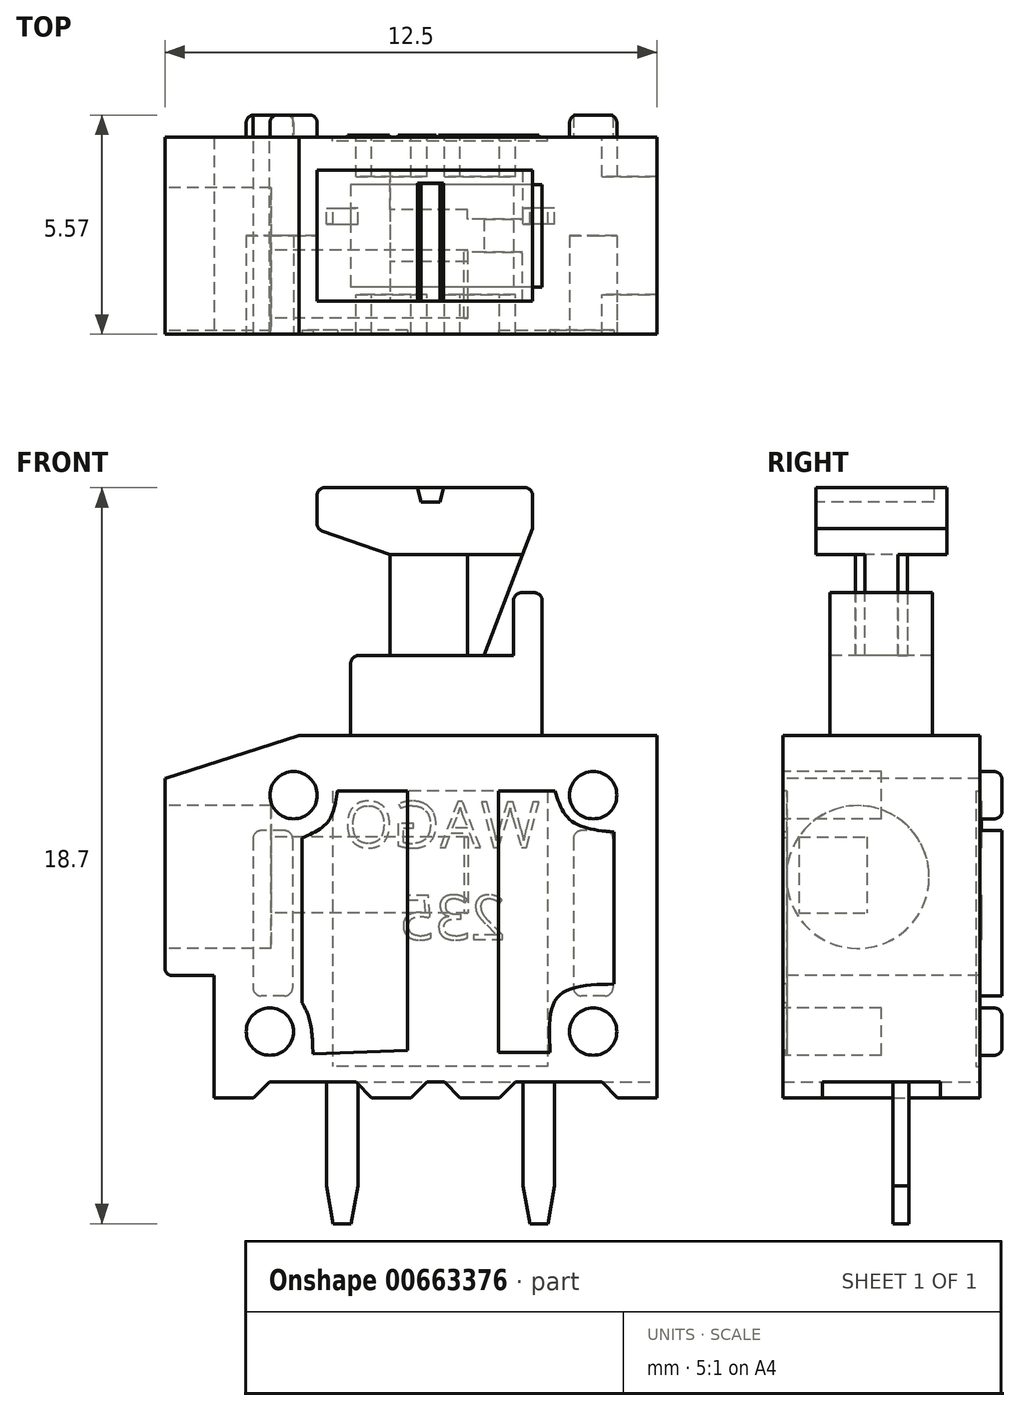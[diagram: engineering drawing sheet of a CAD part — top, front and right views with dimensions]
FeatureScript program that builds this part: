
annotation { "Feature Type Name" : "Feature", "Feature Type Description" : "" }
export const myFeature = defineFeature(function(context is Context, id is Id, definition is map)
    precondition{}
    {
        {
            var Q0;
            Q0=qCreatedBy(makeId("Front.planeOp"),FACE);
            var sketch = newSketch(context, id + "F0", { "sketchPlane" : qUnion([Q0])});
            skLineSegment(sketch, "E0", {"start": v(-5.72, 0) * mm, "end": v(6.78, 0) * mm});
            skLineSegment(sketch, "E1", {"start": v(6.78, 0) * mm, "end": v(6.78, 9.2) * mm});
            skLineSegment(sketch, "E2", {"start": v(6.78, 9.2) * mm, "end": v(-2.3, 9.2) * mm});
            skLineSegment(sketch, "E3", {"start": v(-2.3, 9.2) * mm, "end": v(-5.72, 8.11) * mm});
            skLineSegment(sketch, "E4", {"start": v(-5.72, 8.11) * mm, "end": v(-5.72, 3.1) * mm});
            skLineSegment(sketch, "E5", {"start": v(-5.72, 3.1) * mm, "end": v(-4.47, 3.1) * mm});
            skLineSegment(sketch, "E6", {"start": v(-4.47, 3.1) * mm, "end": v(-4.47, 0) * mm});
            skLineSegment(sketch, "E7", {"start": v(-4.47, 0) * mm, "end": v(6.78, 0) * mm});
            skLineSegment(sketch, "E8", {"start": v(-1, 9.2) * mm, "end": v(-1, 11.23) * mm});
            skLineSegment(sketch, "E9", {"start": v(-1, 11.23) * mm, "end": v(3.14, 11.23) * mm});
            skLineSegment(sketch, "E10", {"start": v(3.14, 11.23) * mm, "end": v(3.14, 12.83) * mm});
            skLineSegment(sketch, "E11", {"start": v(3.14, 12.83) * mm, "end": v(3.86, 12.83) * mm});
            skLineSegment(sketch, "E12", {"start": v(3.86, 12.83) * mm, "end": v(3.86, 9.2) * mm});
            skCircle(sketch, "E13", {"center": v(-2.45, 7.69) * mm, "radius": 0.6 * mm});
            skPoint(sketch, "E13.first.point", {"position": v(-3.05, 7.71) * mm});
            skPoint(sketch, "E13.second.point", {"position": v(-1.86, 7.8) * mm});
            skPoint(sketch, "E13.third.point", {"position": v(-2.42, 8.28) * mm});
            skCircle(sketch, "E14", {"center": v(5.16, 7.69) * mm, "radius": 0.6 * mm});
            skPoint(sketch, "E14.first.point", {"position": v(5.2, 8.28) * mm});
            skPoint(sketch, "E14.second.point", {"position": v(5.13, 7.09) * mm});
            skPoint(sketch, "E14.third.point", {"position": v(5.73, 7.49) * mm});
            skCircle(sketch, "E15", {"center": v(-3.05, 1.68) * mm, "radius": 0.6 * mm});
            skPoint(sketch, "E15.first.point", {"position": v(-3.06, 1.08) * mm});
            skPoint(sketch, "E15.second.point", {"position": v(-3.06, 2.28) * mm});
            skPoint(sketch, "E15.third.point", {"position": v(-3.65, 1.6) * mm});
            skCircle(sketch, "E16", {"center": v(5.16, 1.68) * mm, "radius": 0.6 * mm});
            skPoint(sketch, "E16.first.point", {"position": v(5.08, 2.27) * mm});
            skPoint(sketch, "E16.second.point", {"position": v(5.27, 1.09) * mm});
            skPoint(sketch, "E16.third.point", {"position": v(4.57, 1.6) * mm});
            skLineSegment(sketch, "E17", {"start": v(0.44, 1.2) * mm, "end": v(0.44, 7.8) * mm});
            skLineSegment(sketch, "E18", {"start": v(0.44, 7.8) * mm, "end": v(-1.34, 7.8) * mm});
            skLineSegment(sketch, "E19", {"start": v(-2.24, 6.6) * mm, "end": v(-2.24, 2.41) * mm});
            skLineSegment(sketch, "E20", {"start": v(0.44, 1.2) * mm, "end": v(-1.96, 1.12) * mm});
            skLineSegment(sketch, "E21", {"start": v(2.75, 7.8) * mm, "end": v(2.75, 1.15) * mm});
            skLineSegment(sketch, "E22", {"start": v(2.75, 1.15) * mm, "end": v(4.07, 1.15) * mm});
            skLineSegment(sketch, "E23", {"start": v(2.75, 7.8) * mm, "end": v(4.2, 7.8) * mm});
            skLineSegment(sketch, "E24", {"start": v(5.69, 6.75) * mm, "end": v(5.69, 2.89) * mm});
            skFitSpline(sketch, "E25", {"points": [v(-1.34, 7.8) * mm, v(-1.56, 7.03) * mm, v(-2.24, 6.6) * mm], "startDerivative": vector(-0.32, -1.71) * mm, "endDerivative": vector(-1.56, -0.7) * mm});
            skFitSpline(sketch, "E26", {"points": [v(4.2, 7.8) * mm, v(4.61, 7.03) * mm, v(5.69, 6.75) * mm], "startDerivative": vector(0.5, -1.92) * mm, "endDerivative": vector(2.34, -0.23) * mm});
            skFitSpline(sketch, "E27", {"points": [v(-2.24, 2.41) * mm, v(-2.04, 1.98) * mm, v(-1.96, 1.12) * mm], "startDerivative": vector(0.52, -0.92) * mm, "endDerivative": vector(0.06, -1.73) * mm});
            skFitSpline(sketch, "E28", {"points": [v(5.69, 2.89) * mm, v(4.28, 2.57) * mm, v(4.07, 1.15) * mm], "startDerivative": vector(-3.33, -0.06) * mm, "endDerivative": vector(0.17, -3.39) * mm});
            skLineSegment(sketch, "E29", {"start": v(0, 11.23) * mm, "end": v(0, 13.8) * mm});
            skLineSegment(sketch, "E30", {"start": v(0, 13.8) * mm, "end": v(-1.86, 14.45) * mm});
            skLineSegment(sketch, "E31", {"start": v(-1.86, 14.45) * mm, "end": v(-1.86, 15.5) * mm});
            skLineSegment(sketch, "E32", {"start": v(-1.86, 15.5) * mm, "end": v(3.62, 15.5) * mm});
            skLineSegment(sketch, "E33", {"start": v(3.62, 15.5) * mm, "end": v(3.62, 14.46) * mm});
            skLineSegment(sketch, "E34", {"start": v(3.62, 14.46) * mm, "end": v(2.38, 11.23) * mm});
            skLineSegment(sketch, "E35", {"start": v(2.38, 11.23) * mm, "end": v(1.77, 11.23) * mm});
            skLineSegment(sketch, "E36", {"start": v(1.77, 11.23) * mm, "end": v(1.77, 13.8) * mm});
            skLineSegment(sketch, "E37", {"start": v(1.77, 13.8) * mm, "end": v(0, 13.8) * mm});
            skLineSegment(sketch, "E38", {"start": v(1.77, 13.8) * mm, "end": v(3.62, 14.46) * mm});
            skSolve(sketch);
        }
        {
            var Q0;
            {var subQ4=sQuery(id+"F0.wireOp",EDGE,"E1");Q0=makeQuery(id+"F0.imprint","IMPRINT",FACE,{"disambiguationData":[TD([[makeQuery(id+"F0.imprint","IMPRINT",EDGE,{"derivedFrom":subQ4}),1.0]])]});}
            var Q1;
            Q1=makeQuery(id+"F0.imprint","IMPRINT",FACE,{"disambiguationData":[TD([[makeQuery(id+"F0.imprint","IMPRINT",EDGE,{"derivedFrom":sQuery(id+"F0.wireOp",EDGE,"E17")}),1.0]])]});
            var Q2;
            Q2=makeQuery(id+"F0.imprint","IMPRINT",FACE,{"disambiguationData":[TD([[makeQuery(id+"F0.imprint","IMPRINT",EDGE,{"derivedFrom":sQuery(id+"F0.wireOp",EDGE,"E21")}),1.0]])]});
            var Q3;
            {var subQ3=sQuery(id+"F0.wireOp",EDGE,"E8");Q3=makeQuery(id+"F0.imprint","IMPRINT",FACE,{"disambiguationData":[TD([[makeQuery(id+"F0.imprint","IMPRINT",EDGE,{"derivedFrom":subQ3}),-1.0]])]});}
            var Q4;
            Q4=makeQuery(id+"F0.imprint","IMPRINT",FACE,{"disambiguationData":[TD([[makeQuery(id+"F0.imprint","IMPRINT",EDGE,{"derivedFrom":sQuery(id+"F0.wireOp",EDGE,"E13")}),1.0]])]});
            var Q5;
            Q5=makeQuery(id+"F0.imprint","IMPRINT",FACE,{"disambiguationData":[TD([[makeQuery(id+"F0.imprint","IMPRINT",EDGE,{"derivedFrom":sQuery(id+"F0.wireOp",EDGE,"E14")}),1.0]])]});
            var Q6;
            Q6=makeQuery(id+"F0.imprint","IMPRINT",FACE,{"disambiguationData":[TD([[makeQuery(id+"F0.imprint","IMPRINT",EDGE,{"derivedFrom":sQuery(id+"F0.wireOp",EDGE,"E16")}),1.0]])]});
            var Q7;
            Q7=makeQuery(id+"F0.imprint","IMPRINT",FACE,{"disambiguationData":[TD([[makeQuery(id+"F0.imprint","IMPRINT",EDGE,{"derivedFrom":sQuery(id+"F0.wireOp",EDGE,"E15")}),1.0]])]});
            extrude(context, id + "F1", {"entities" : qUnion([Q0, Q1, Q2, Q3, Q4, Q5, Q6, Q7]), "oppositeDirection" : true, "depth" : 5 * mm, "offsetDistance" : 25 * mm});
        }
        {
            var Q0;
            Q0=makeQuery(id+"F0.imprint","IMPRINT",FACE,{"disambiguationData":[TD([[makeQuery(id+"F0.imprint","IMPRINT",EDGE,{"derivedFrom":sQuery(id+"F0.wireOp",EDGE,"E17")}),1.0]])]});
            var Q1;
            Q1=makeQuery(id+"F0.imprint","IMPRINT",FACE,{"disambiguationData":[TD([[makeQuery(id+"F0.imprint","IMPRINT",EDGE,{"derivedFrom":sQuery(id+"F0.wireOp",EDGE,"E21")}),1.0]])]});
            extrude(context, id + "F2", {"entities" : qUnion([Q0, Q1]), "operationType" : NewBodyOperationType.REMOVE, "oppositeDirection" : true, "depth" : 0.1 * mm, "offsetDistance" : 25 * mm});
        }
        {
            var Q0;
            Q0=makeQuery(id+"F0.imprint","IMPRINT",FACE,{"disambiguationData":[TD([[makeQuery(id+"F0.imprint","IMPRINT",EDGE,{"derivedFrom":sQuery(id+"F0.wireOp",EDGE,"E13")}),1.0]])]});
            var Q1;
            Q1=makeQuery(id+"F0.imprint","IMPRINT",FACE,{"disambiguationData":[TD([[makeQuery(id+"F0.imprint","IMPRINT",EDGE,{"derivedFrom":sQuery(id+"F0.wireOp",EDGE,"E14")}),1.0]])]});
            var Q2;
            Q2=makeQuery(id+"F0.imprint","IMPRINT",FACE,{"disambiguationData":[TD([[makeQuery(id+"F0.imprint","IMPRINT",EDGE,{"derivedFrom":sQuery(id+"F0.wireOp",EDGE,"E16")}),1.0]])]});
            var Q3;
            Q3=makeQuery(id+"F0.imprint","IMPRINT",FACE,{"disambiguationData":[TD([[makeQuery(id+"F0.imprint","IMPRINT",EDGE,{"derivedFrom":sQuery(id+"F0.wireOp",EDGE,"E15")}),1.0]])]});
            extrude(context, id + "F3", {"entities" : qUnion([Q0, Q1, Q2, Q3]), "operationType" : NewBodyOperationType.REMOVE, "oppositeDirection" : true, "depth" : 2.5 * mm, "offsetDistance" : 25 * mm});
        }
        {
            var Q0;
            {var subQ0=sQuery(id+"F0.wireOp",EDGE,"E29");Q0=makeQuery(id+"F0.imprint","IMPRINT",FACE,{"disambiguationData":[TD([[makeQuery(id+"F0.imprint","IMPRINT",EDGE,{"derivedFrom":subQ0}),-1.0]])]});}
            var Q1;
            Q1=makeQuery(id+"F0.imprint","IMPRINT",FACE,{"disambiguationData":[TD([[makeQuery(id+"F0.imprint","IMPRINT",EDGE,{"derivedFrom":sQuery(id+"F0.wireOp",EDGE,"E30")}),-1.0]])]});
            var Q2;
            Q2=makeQuery(id+"F0.imprint","IMPRINT",FACE,{"disambiguationData":[TD([[makeQuery(id+"F0.imprint","IMPRINT",EDGE,{"derivedFrom":sQuery(id+"F0.wireOp",EDGE,"E34")}),-1.0]])]});
            extrude(context, id + "F4", {"entities" : qUnion([Q0, Q1, Q2]), "oppositeDirection" : true, "depth" : 5 * mm, "offsetDistance" : 25 * mm});
        }
        {
            var Q0;
            Q0=makeQuery(id+"F0.imprint","IMPRINT",FACE,{"disambiguationData":[TD([[makeQuery(id+"F0.imprint","IMPRINT",EDGE,{"derivedFrom":sQuery(id+"F0.wireOp",EDGE,"E13")}),1.0]])]});
            var Q1;
            Q1=makeQuery(id+"F0.imprint","IMPRINT",FACE,{"disambiguationData":[TD([[makeQuery(id+"F0.imprint","IMPRINT",EDGE,{"derivedFrom":sQuery(id+"F0.wireOp",EDGE,"E14")}),1.0]])]});
            var Q2;
            Q2=makeQuery(id+"F0.imprint","IMPRINT",FACE,{"disambiguationData":[TD([[makeQuery(id+"F0.imprint","IMPRINT",EDGE,{"derivedFrom":sQuery(id+"F0.wireOp",EDGE,"E16")}),1.0]])]});
            var Q3;
            Q3=makeQuery(id+"F0.imprint","IMPRINT",FACE,{"disambiguationData":[TD([[makeQuery(id+"F0.imprint","IMPRINT",EDGE,{"derivedFrom":sQuery(id+"F0.wireOp",EDGE,"E15")}),1.0]])]});
            extrude(context, id + "F5", {"entities" : qUnion([Q0, Q1, Q2, Q3]), "operationType" : NewBodyOperationType.ADD, "oppositeDirection" : true, "depth" : 5.57 * mm, "offsetDistance" : 25 * mm});
        }
        {
            var Q0;
            Q0=makeQuery(id+"F0.imprint","IMPRINT",FACE,{"disambiguationData":[TD([[makeQuery(id+"F0.imprint","IMPRINT",EDGE,{"derivedFrom":sQuery(id+"F0.wireOp",EDGE,"E13")}),1.0]])]});
            var Q1;
            Q1=makeQuery(id+"F0.imprint","IMPRINT",FACE,{"disambiguationData":[TD([[makeQuery(id+"F0.imprint","IMPRINT",EDGE,{"derivedFrom":sQuery(id+"F0.wireOp",EDGE,"E14")}),1.0]])]});
            var Q2;
            Q2=makeQuery(id+"F0.imprint","IMPRINT",FACE,{"disambiguationData":[TD([[makeQuery(id+"F0.imprint","IMPRINT",EDGE,{"derivedFrom":sQuery(id+"F0.wireOp",EDGE,"E15")}),1.0]])]});
            var Q3;
            Q3=makeQuery(id+"F0.imprint","IMPRINT",FACE,{"disambiguationData":[TD([[makeQuery(id+"F0.imprint","IMPRINT",EDGE,{"derivedFrom":sQuery(id+"F0.wireOp",EDGE,"E16")}),1.0]])]});
            extrude(context, id + "F6", {"entities" : qUnion([Q0, Q1, Q2, Q3]), "operationType" : NewBodyOperationType.REMOVE, "oppositeDirection" : true, "depth" : 2.5 * mm, "offsetDistance" : 25 * mm});
        }
        {
            var Q0;
            Q0=makeQuery(id+"F1.opExtrude","SWEPT_FACE",FACE,{"disambiguationData":[OSD([sQuery(id+"F0.wireOp",EDGE,"E4")])]});
            var sketch = newSketch(context, id + "F7", { "sketchPlane" : qUnion([Q0])});
            skPoint(sketch, "E39.first.point", {"position": v(0, 5.6) * mm});
            skPoint(sketch, "E39.second.point.positionSnap0", {"position": v(0, 5.6) * mm});
            skLineSegment(sketch, "E40.bottom", {"start": v(-5, 8.11) * mm, "end": v(0, 8.11) * mm});
            skLineSegment(sketch, "E40.top", {"start": v(-5, 15.5) * mm, "end": v(0, 15.5) * mm});
            skLineSegment(sketch, "E40.left", {"start": v(-5, 8.11) * mm, "end": v(-5, 15.5) * mm});
            skLineSegment(sketch, "E40.right", {"start": v(0, 8.11) * mm, "end": v(0, 15.5) * mm});
            skLineSegment(sketch, "E41.bottom", {"start": v(-5, 9.2) * mm, "end": v(-3.8, 9.2) * mm});
            skLineSegment(sketch, "E41.top", {"start": v(-5, 13.8) * mm, "end": v(-3.8, 13.8) * mm});
            skLineSegment(sketch, "E41.left", {"start": v(-5, 9.2) * mm, "end": v(-5, 13.8) * mm});
            skLineSegment(sketch, "E41.right", {"start": v(-3.8, 9.2) * mm, "end": v(-3.8, 13.8) * mm});
            skLineSegment(sketch, "E42.bottom", {"start": v(0, 9.2) * mm, "end": v(-1.2, 9.2) * mm});
            skLineSegment(sketch, "E42.top", {"start": v(0, 13.8) * mm, "end": v(-1.2, 13.8) * mm});
            skLineSegment(sketch, "E42.left", {"start": v(0, 9.2) * mm, "end": v(0, 13.8) * mm});
            skLineSegment(sketch, "E42.right", {"start": v(-1.2, 9.2) * mm, "end": v(-1.2, 13.8) * mm});
            skCircle(sketch, "E43", {"center": v(-1.9, 5.6) * mm, "radius": 1.81 * mm});
            skPoint(sketch, "E43.first.point", {"position": v(-0.09, 5.6) * mm});
            skPoint(sketch, "E43.second.point", {"position": v(-3.72, 5.6) * mm});
            skPoint(sketch, "E43.third.point", {"position": v(-1.92, 7.42) * mm});
            skSolve(sketch);
        }
        {
            var Q0;
            Q0=makeQuery(id+"F7.imprint","IMPRINT",FACE,{"disambiguationData":[TD([[makeQuery(id+"F7.imprint","IMPRINT",EDGE,{"derivedFrom":sQuery(id+"F7.wireOp",EDGE,"E43")}),1.0]])]});
            extrude(context, id + "F8", {"entities" : qUnion([Q0]), "operationType" : NewBodyOperationType.REMOVE, "oppositeDirection" : true, "depth" : 2.7 * mm, "offsetDistance" : 25 * mm});
        }
        {
            var Q0;
            Q0=makeQuery(id+"F7.imprint","IMPRINT",FACE,{"disambiguationData":[TD([[makeQuery(id+"F7.imprint","IMPRINT",EDGE,{"derivedFrom":sQuery(id+"F7.wireOp",EDGE,"E41.bottom")}),1.0]])]});
            var Q1;
            Q1=makeQuery(id+"F7.imprint","IMPRINT",FACE,{"disambiguationData":[TD([[makeQuery(id+"F7.imprint","IMPRINT",EDGE,{"derivedFrom":sQuery(id+"F7.wireOp",EDGE,"E42.bottom")}),-1.0]])]});
            extrude(context, id + "F9", {"entities" : qUnion([Q0, Q1]), "operationType" : NewBodyOperationType.REMOVE, "oppositeDirection" : true, "depth" : 25 * mm, "offsetDistance" : 25 * mm});
        }
        {
            var Q0;
            Q0=makeQuery(id+"F9.boolean.opBoolean","COPY",FACE,{"disambiguationData":[TD([makeQuery(id+"F4.opExtrude","SWEPT_FACE",FACE,{"disambiguationData":[OSD([sQuery(id+"F0.wireOp",EDGE,"E29")])]})])],"derivedFrom":makeQuery(id+"F9.opExtrude","SWEPT_FACE",FACE,{"disambiguationData":[OSD([sQuery(id+"F7.wireOp",EDGE,"E42.right")])]})});
            extrude(context, id + "F10", {"entities" : qUnion([Q0]), "operationType" : NewBodyOperationType.REMOVE, "oppositeDirection" : true, "depth" : 0.64 * mm, "offsetDistance" : 25 * mm});
        }
        {
            var Q0;
            Q0=makeQuery(id+"F9.boolean.opBoolean","COPY",FACE,{"disambiguationData":[TD([makeQuery(id+"F4.opExtrude","SWEPT_FACE",FACE,{"disambiguationData":[OSD([sQuery(id+"F0.wireOp",EDGE,"E29")])]})])],"derivedFrom":makeQuery(id+"F9.opExtrude","SWEPT_FACE",FACE,{"disambiguationData":[OSD([sQuery(id+"F7.wireOp",EDGE,"E41.right")])]})});
            extrude(context, id + "F11", {"entities" : qUnion([Q0]), "operationType" : NewBodyOperationType.REMOVE, "oppositeDirection" : true, "depth" : 0.64 * mm, "offsetDistance" : 25 * mm});
        }
        {
            var Q0;
            Q0=makeQuery(id+"F4.opExtrude","CAP_FACE",FACE,{"disambiguationData":[OSD([sQuery(id+"F0.wireOp",EDGE,"E9"),sQuery(id+"F0.wireOp",EDGE,"E29"),sQuery(id+"F0.wireOp",EDGE,"E30"),sQuery(id+"F0.wireOp",EDGE,"E31"),sQuery(id+"F0.wireOp",EDGE,"E32"),sQuery(id+"F0.wireOp",EDGE,"E33"),sQuery(id+"F0.wireOp",EDGE,"E34"),sQuery(id+"F0.wireOp",EDGE,"E35")])],"isStart":false});
            extrude(context, id + "F12", {"entities" : qUnion([Q0]), "operationType" : NewBodyOperationType.REMOVE, "oppositeDirection" : true, "depth" : 0.83 * mm, "offsetDistance" : 25 * mm});
        }
        {
            var Q0;
            Q0=makeQuery(id+"F4.opExtrude","CAP_FACE",FACE,{"disambiguationData":[OSD([sQuery(id+"F0.wireOp",EDGE,"E9"),sQuery(id+"F0.wireOp",EDGE,"E29"),sQuery(id+"F0.wireOp",EDGE,"E30"),sQuery(id+"F0.wireOp",EDGE,"E31"),sQuery(id+"F0.wireOp",EDGE,"E32"),sQuery(id+"F0.wireOp",EDGE,"E33"),sQuery(id+"F0.wireOp",EDGE,"E34"),sQuery(id+"F0.wireOp",EDGE,"E35")])],"isStart":true});
            extrude(context, id + "F13", {"entities" : qUnion([Q0]), "operationType" : NewBodyOperationType.REMOVE, "oppositeDirection" : true, "depth" : 0.83 * mm, "offsetDistance" : 25 * mm});
        }
        {
            var Q0;
            Q0=makeQuery(id+"F13.boolean.opBoolean","COPY",FACE,{"derivedFrom":makeQuery(id+"F13.opExtrude","CAP_FACE",FACE,{"disambiguationData":[OSD([sQuery(id+"F0.wireOp",EDGE,"E9"),sQuery(id+"F0.wireOp",EDGE,"E29"),sQuery(id+"F0.wireOp",EDGE,"E30"),sQuery(id+"F0.wireOp",EDGE,"E31"),sQuery(id+"F0.wireOp",EDGE,"E32"),sQuery(id+"F0.wireOp",EDGE,"E33"),sQuery(id+"F0.wireOp",EDGE,"E34"),sQuery(id+"F0.wireOp",EDGE,"E35")])],"isStart":false})});
            var sketch = newSketch(context, id + "F14", { "sketchPlane" : qUnion([Q0])});
            skLineSegment(sketch, "E44", {"start": v(0.7, 15.5) * mm, "end": v(0.8, 15.13) * mm});
            skLineSegment(sketch, "E45", {"start": v(0.8, 15.13) * mm, "end": v(1.03, 15.13) * mm});
            skLineSegment(sketch, "E46.MirrorCS", {"start": v(1.27, 15.13) * mm, "end": v(1.03, 15.13) * mm});
            skLineSegment(sketch, "E47.MirrorCS", {"start": v(1.36, 15.5) * mm, "end": v(1.27, 15.13) * mm});
            skLineSegment(sketch, "E48", {"start": v(0.7, 15.5) * mm, "end": v(1.36, 15.5) * mm});
            skSolve(sketch);
        }
        {
            var Q0;
            Q0=makeQuery(id+"F14.imprint","IMPRINT",FACE,{"disambiguationData":[TD([[makeQuery(id+"F14.imprint","IMPRINT",EDGE,{"derivedFrom":sQuery(id+"F14.wireOp",EDGE,"E44")}),1.0]])]});
            extrude(context, id + "F15", {"entities" : qUnion([Q0]), "operationType" : NewBodyOperationType.REMOVE, "oppositeDirection" : true, "depth" : 3 * mm, "offsetDistance" : 25 * mm});
        }
        {
            var Q0;
            Q0=makeQuery(id+"F10.boolean.opBoolean","COPY",FACE,{"derivedFrom":makeQuery(id+"F10.opExtrude","CAP_FACE",FACE,{"disambiguationData":[OSD([sQuery(id+"F7.wireOp",EDGE,"E42.right")])],"isStart":false})});
            var sketch = newSketch(context, id + "F16", { "sketchPlane" : qUnion([Q0])});
            skLineSegment(sketch, "E49", {"start": v(2.38, 11.23) * mm, "end": v(1.97, 11.23) * mm});
            skLineSegment(sketch, "E50", {"start": v(1.97, 11.23) * mm, "end": v(1.97, 13.8) * mm});
            skLineSegment(sketch, "E51", {"start": v(1.97, 13.8) * mm, "end": v(3.37, 13.8) * mm});
            skLineSegment(sketch, "E52", {"start": v(3.37, 13.8) * mm, "end": v(2.38, 11.23) * mm});
            skSolve(sketch);
        }
        {
            var Q0;
            Q0=makeQuery(id+"F16.imprint","IMPRINT",FACE,{"disambiguationData":[TD([[makeQuery(id+"F16.imprint","IMPRINT",EDGE,{"derivedFrom":sQuery(id+"F16.wireOp",EDGE,"E49")}),-1.0]])]});
            extrude(context, id + "F17", {"entities" : qUnion([Q0]), "operationType" : NewBodyOperationType.REMOVE, "oppositeDirection" : true, "depth" : 0.24 * mm, "offsetDistance" : 25 * mm});
        }
        {
            var Q0;
            Q0=makeQuery(id+"F11.boolean.opBoolean","COPY",FACE,{"derivedFrom":makeQuery(id+"F11.opExtrude","CAP_FACE",FACE,{"disambiguationData":[OSD([sQuery(id+"F7.wireOp",EDGE,"E41.right")])],"isStart":false})});
            var sketch = newSketch(context, id + "F18", { "sketchPlane" : qUnion([Q0])});
            skLineSegment(sketch, "E53", {"start": v(-3.37, 13.8) * mm, "end": v(-1.97, 13.8) * mm});
            skLineSegment(sketch, "E54", {"start": v(-1.97, 13.8) * mm, "end": v(-1.97, 11.23) * mm});
            skLineSegment(sketch, "E55", {"start": v(-1.97, 11.23) * mm, "end": v(-2.38, 11.23) * mm});
            skLineSegment(sketch, "E56", {"start": v(-2.38, 11.23) * mm, "end": v(-3.37, 13.8) * mm});
            skSolve(sketch);
        }
        {
            var Q0;
            Q0=makeQuery(id+"F18.imprint","IMPRINT",FACE,{"disambiguationData":[TD([[makeQuery(id+"F18.imprint","IMPRINT",EDGE,{"derivedFrom":sQuery(id+"F18.wireOp",EDGE,"E53")}),-1.0]])]});
            extrude(context, id + "F19", {"entities" : qUnion([Q0]), "operationType" : NewBodyOperationType.REMOVE, "oppositeDirection" : true, "depth" : 0.24 * mm, "offsetDistance" : 25 * mm});
        }
        {
            var Q0;
            Q0=makeQuery(id+"F8.boolean.opBoolean","COPY",FACE,{"derivedFrom":makeQuery(id+"F8.opExtrude","CAP_FACE",FACE,{"disambiguationData":[OSD([sQuery(id+"F7.wireOp",EDGE,"E43")])],"isStart":false})});
            var sketch = newSketch(context, id + "F20", { "sketchPlane" : qUnion([Q0])});
            skLineSegment(sketch, "E57.bottom", {"start": v(-0.4, 6.63) * mm, "end": v(-2.14, 6.63) * mm});
            skLineSegment(sketch, "E57.top", {"start": v(-0.4, 4.7) * mm, "end": v(-2.14, 4.7) * mm});
            skLineSegment(sketch, "E57.left", {"start": v(-0.4, 6.63) * mm, "end": v(-0.4, 4.7) * mm});
            skLineSegment(sketch, "E57.right", {"start": v(-2.14, 6.63) * mm, "end": v(-2.14, 4.7) * mm});
            skSolve(sketch);
        }
        {
            var Q0;
            Q0=makeQuery(id+"F20.imprint","IMPRINT",FACE,{"disambiguationData":[TD([[makeQuery(id+"F20.imprint","IMPRINT",EDGE,{"derivedFrom":sQuery(id+"F20.wireOp",EDGE,"E57.bottom")}),1.0]])]});
            extrude(context, id + "F21", {"entities" : qUnion([Q0]), "operationType" : NewBodyOperationType.REMOVE, "oppositeDirection" : true, "depth" : 5 * mm, "offsetDistance" : 25 * mm});
        }
        {
            var Q0;
            Q0=makeQuery(id+"F1.opExtrude","CAP_FACE",FACE,{"disambiguationData":[OSD([sQuery(id+"F0.wireOp",EDGE,"E1"),sQuery(id+"F0.wireOp",EDGE,"E2"),sQuery(id+"F0.wireOp",EDGE,"E3"),sQuery(id+"F0.wireOp",EDGE,"E4"),sQuery(id+"F0.wireOp",EDGE,"E5"),sQuery(id+"F0.wireOp",EDGE,"E6"),sQuery(id+"F0.wireOp",EDGE,"E7"),sQuery(id+"F0.wireOp",EDGE,"E8"),sQuery(id+"F0.wireOp",EDGE,"E9"),sQuery(id+"F0.wireOp",EDGE,"E10"),sQuery(id+"F0.wireOp",EDGE,"E11"),sQuery(id+"F0.wireOp",EDGE,"E12"),sQuery(id+"F0.wireOp",EDGE,"E35")])],"isStart":false});
            var sketch = newSketch(context, id + "F22", { "sketchPlane" : qUnion([Q0])});
            skLineSegment(sketch, "E58.bottom", {"start": v(-5.66, 6.79) * mm, "end": v(-4.66, 6.79) * mm});
            skLineSegment(sketch, "E58.top", {"start": v(-5.66, 2.59) * mm, "end": v(-4.66, 2.59) * mm});
            skLineSegment(sketch, "E58.left", {"start": v(-5.66, 6.79) * mm, "end": v(-5.66, 2.59) * mm});
            skLineSegment(sketch, "E58.right", {"start": v(-4.66, 6.79) * mm, "end": v(-4.66, 2.59) * mm});
            skLineSegment(sketch, "E59.bottom", {"start": v(2.48, 6.79) * mm, "end": v(3.48, 6.79) * mm});
            skLineSegment(sketch, "E59.top", {"start": v(2.48, 2.59) * mm, "end": v(3.48, 2.59) * mm});
            skLineSegment(sketch, "E59.left", {"start": v(2.48, 6.79) * mm, "end": v(2.48, 2.59) * mm});
            skLineSegment(sketch, "E59.right", {"start": v(3.48, 6.79) * mm, "end": v(3.48, 2.59) * mm});
            skLineSegment(sketch, "E60.bottom", {"start": v(-4, 7.8) * mm, "end": v(1.46, 7.8) * mm});
            skLineSegment(sketch, "E60.top", {"start": v(-4, 0.8) * mm, "end": v(1.46, 0.8) * mm});
            skLineSegment(sketch, "E60.left", {"start": v(-4, 7.8) * mm, "end": v(-4, 0.8) * mm});
            skLineSegment(sketch, "E60.right", {"start": v(1.46, 7.8) * mm, "end": v(1.46, 0.8) * mm});
            skLineSegment(sketch, "E61", {"start": v(-5.78, 0) * mm, "end": v(-5.38, 0.4) * mm});
            skLineSegment(sketch, "E62", {"start": v(-5.38, 0.4) * mm, "end": v(-3.18, 0.4) * mm});
            skLineSegment(sketch, "E63", {"start": v(-3.18, 0.4) * mm, "end": v(-2.78, 0) * mm});
            skLineSegment(sketch, "E64", {"start": v(-2.78, 0) * mm, "end": v(-1.78, 0) * mm});
            skLineSegment(sketch, "E65", {"start": v(-1.78, 0) * mm, "end": v(-1.38, 0.4) * mm});
            skLineSegment(sketch, "E66", {"start": v(-1.38, 0.4) * mm, "end": v(-0.93, 0.4) * mm});
            skLineSegment(sketch, "E67", {"start": v(-0.93, 0.4) * mm, "end": v(-0.53, 0) * mm});
            skLineSegment(sketch, "E68", {"start": v(-0.53, 0) * mm, "end": v(0.47, 0) * mm});
            skLineSegment(sketch, "E69", {"start": v(0.47, 0) * mm, "end": v(0.87, 0.4) * mm});
            skLineSegment(sketch, "E70", {"start": v(0.87, 0.4) * mm, "end": v(3.07, 0.4) * mm});
            skLineSegment(sketch, "E71", {"start": v(3.07, 0.4) * mm, "end": v(3.47, 0) * mm});
            skSolve(sketch);
        }
        {
            var Q0;
            Q0=makeQuery(id+"F22.imprint","IMPRINT",FACE,{"disambiguationData":[TD([[makeQuery(id+"F22.imprint","IMPRINT",EDGE,{"derivedFrom":sQuery(id+"F22.wireOp",EDGE,"E58.bottom")}),-1.0]])]});
            var Q1;
            Q1=makeQuery(id+"F22.imprint","IMPRINT",FACE,{"disambiguationData":[TD([[makeQuery(id+"F22.imprint","IMPRINT",EDGE,{"derivedFrom":sQuery(id+"F22.wireOp",EDGE,"E59.bottom")}),-1.0]])]});
            extrude(context, id + "F23", {"entities" : qUnion([Q0, Q1]), "operationType" : NewBodyOperationType.ADD, "depth" : 0.57 * mm, "offsetDistance" : 25 * mm});
        }
        {
            var Q0;
            Q0=makeQuery(id+"F22.imprint","IMPRINT",FACE,{"disambiguationData":[TD([[makeQuery(id+"F22.imprint","IMPRINT",EDGE,{"derivedFrom":sQuery(id+"F22.wireOp",EDGE,"E60.bottom")}),-1.0]])]});
            extrude(context, id + "F24", {"entities" : qUnion([Q0]), "operationType" : NewBodyOperationType.REMOVE, "oppositeDirection" : true, "depth" : 0.1 * mm, "offsetDistance" : 25 * mm});
        }
        {
            var Q0;
            {var subQ0=sQuery(id+"F22.wireOp",EDGE,"E61");Q0=makeQuery(id+"F22.imprint","IMPRINT",FACE,{"disambiguationData":[TD([[makeQuery(id+"F22.imprint","IMPRINT",EDGE,{"derivedFrom":subQ0}),-1.0]])]});}
            var Q1;
            {var subQ0=sQuery(id+"F22.wireOp",EDGE,"E65");Q1=makeQuery(id+"F22.imprint","IMPRINT",FACE,{"disambiguationData":[TD([[makeQuery(id+"F22.imprint","IMPRINT",EDGE,{"derivedFrom":subQ0}),-1.0]])]});}
            var Q2;
            {var subQ0=sQuery(id+"F22.wireOp",EDGE,"E69");Q2=makeQuery(id+"F22.imprint","IMPRINT",FACE,{"disambiguationData":[TD([[makeQuery(id+"F22.imprint","IMPRINT",EDGE,{"derivedFrom":subQ0}),-1.0]])]});}
            extrude(context, id + "F25", {"entities" : qUnion([Q0, Q1, Q2]), "operationType" : NewBodyOperationType.REMOVE, "oppositeDirection" : true, "depth" : 5 * mm, "offsetDistance" : 25 * mm});
        }
        {
            var Q0;
            Q0=makeQuery(id+"F1.opExtrude","SWEPT_FACE",FACE,{"disambiguationData":[OSD([sQuery(id+"F0.wireOp",EDGE,"E1")])]});
            var sketch = newSketch(context, id + "F26", { "sketchPlane" : qUnion([Q0])});
            skLineSegment(sketch, "E72.bottom", {"start": v(1, 0.4) * mm, "end": v(4, 0.4) * mm});
            skLineSegment(sketch, "E72.top", {"start": v(1, -0.4) * mm, "end": v(4, -0.4) * mm});
            skLineSegment(sketch, "E72.left", {"start": v(1, 0.4) * mm, "end": v(1, -0.4) * mm});
            skLineSegment(sketch, "E72.right", {"start": v(4, 0.4) * mm, "end": v(4, -0.4) * mm});
            skPoint(sketch, "E72.middle", {"position": v(2.5, 0) * mm});
            skSolve(sketch);
        }
        {
            var Q0;
            Q0 = qSketchRegion(id + "F26", true);
            extrude(context, id + "F27", {"entities" : qUnion([Q0]), "operationType" : NewBodyOperationType.REMOVE, "oppositeDirection" : true, "depth" : 8 * mm, "offsetDistance" : 25 * mm});
        }
        {
            var Q0;
            Q0=makeQuery(id+"F22.imprint","IMPRINT",FACE,{"disambiguationData":[TD([[makeQuery(id+"F22.imprint","IMPRINT",EDGE,{"derivedFrom":sQuery(id+"F22.wireOp",EDGE,"E60.bottom")}),-1.0]])]});
            var sketch = newSketch(context, id + "F28", { "sketchPlane" : qUnion([Q0])});
            skText(sketch, "E73", { "text": "WAGO", "fontName": "OpenSans-Regular.ttf"});
            skText(sketch, "E74", { "text": "235", "fontName": "OpenSans-Regular.ttf"});
            const initialGuessF28  = {"E73": [-0.0038, 0.00636, 1, 0, 0.00117], "E74": [-0.00294, 0.00402, 1, 0, 0.00113]};
            skSetInitialGuess(sketch, initialGuessF28);
            skSolve(sketch);
        }
        {
            var Q0;
            Q0 = qSketchRegion(id + "F28", true);
            extrude(context, id + "F29", {"entities" : qUnion([Q0]), "operationType" : NewBodyOperationType.ADD, "depth" : 0.05 * mm, "offsetDistance" : 25 * mm});
        }
        {
            var Q0;
            Q0=makeQuery(id+"F27.boolean.opBoolean","MERGE",FACE,{"derivedFrom":[makeQuery(id+"F25.boolean.opBoolean","COPY",FACE,{"derivedFrom":makeQuery(id+"F25.opExtrude","SWEPT_FACE",FACE,{"disambiguationData":[OSD([sQuery(id+"F22.wireOp",EDGE,"E62")])]})}),makeQuery(id+"F25.boolean.opBoolean","COPY",FACE,{"derivedFrom":makeQuery(id+"F25.opExtrude","SWEPT_FACE",FACE,{"disambiguationData":[OSD([sQuery(id+"F22.wireOp",EDGE,"E66")])]})}),makeQuery(id+"F25.boolean.opBoolean","COPY",FACE,{"derivedFrom":makeQuery(id+"F25.opExtrude","SWEPT_FACE",FACE,{"disambiguationData":[OSD([sQuery(id+"F22.wireOp",EDGE,"E70")])]})}),makeQuery(id+"F27.opExtrude","SWEPT_FACE",FACE,{"disambiguationData":[OSD([sQuery(id+"F26.wireOp",EDGE,"E72.bottom")])]})]});
            var sketch = newSketch(context, id + "F30", { "sketchPlane" : qUnion([Q0])});
            skLineSegment(sketch, "E75.bottom", {"start": v(4.18, -3.2) * mm, "end": v(3.38, -3.2) * mm});
            skLineSegment(sketch, "E75.top", {"start": v(4.18, -2.8) * mm, "end": v(3.38, -2.8) * mm});
            skLineSegment(sketch, "E75.left", {"start": v(4.18, -3.2) * mm, "end": v(4.18, -2.8) * mm});
            skLineSegment(sketch, "E75.right", {"start": v(3.38, -3.2) * mm, "end": v(3.38, -2.8) * mm});
            skPoint(sketch, "E75.middle", {"position": v(3.78, -3) * mm});
            skLineSegment(sketch, "E76.bottom", {"start": v(-1.62, -2.8) * mm, "end": v(-0.82, -2.8) * mm});
            skLineSegment(sketch, "E76.top", {"start": v(-1.62, -3.2) * mm, "end": v(-0.82, -3.2) * mm});
            skLineSegment(sketch, "E76.left", {"start": v(-1.62, -2.8) * mm, "end": v(-1.62, -3.2) * mm});
            skLineSegment(sketch, "E76.right", {"start": v(-0.82, -2.8) * mm, "end": v(-0.82, -3.2) * mm});
            skPoint(sketch, "E76.middle", {"position": v(-1.22, -3) * mm});
            skPoint(sketch, "E76.middle.positionSnap0", {"position": v(4.18, -3) * mm});
            skPoint(sketch, "E76.cornerSnap0", {"position": v(3.78, -2.8) * mm});
            skPoint(sketch, "E76.centerSnap0", {"position": v(4.18, -3) * mm});
            skSolve(sketch);
        }
        {
            var Q0;
            Q0=makeQuery(id+"F30.imprint","IMPRINT",FACE,{"disambiguationData":[TD([[makeQuery(id+"F30.imprint","IMPRINT",EDGE,{"derivedFrom":sQuery(id+"F30.wireOp",EDGE,"E76.bottom")}),-1.0]])]});
            var Q1;
            Q1=makeQuery(id+"F30.imprint","IMPRINT",FACE,{"disambiguationData":[TD([[makeQuery(id+"F30.imprint","IMPRINT",EDGE,{"derivedFrom":sQuery(id+"F30.wireOp",EDGE,"E75.bottom")}),-1.0]])]});
            extrude(context, id + "F31", {"entities" : qUnion([Q0, Q1]), "depth" : 3.6 * mm, "offsetDistance" : 25 * mm});
        }
        {
            var Q0;
            Q0=makeQuery(id+"F21.boolean.opBoolean","COPY",FACE,{"derivedFrom":makeQuery(id+"F21.opExtrude","CAP_FACE",FACE,{"disambiguationData":[OSD([sQuery(id+"F20.wireOp",EDGE,"E57.bottom"),sQuery(id+"F20.wireOp",EDGE,"E57.top"),sQuery(id+"F20.wireOp",EDGE,"E57.left"),sQuery(id+"F20.wireOp",EDGE,"E57.right")])],"isStart":false})});
            extrude(context, id + "F32", {"entities" : qUnion([Q0]), "depth" : 0.1 * mm, "offsetDistance" : 25 * mm});
        }
        {
            var Q0;
            Q0=makeQuery(id+"F31.opExtrude","SWEPT_FACE",FACE,{"disambiguationData":[OSD([sQuery(id+"F30.wireOp",EDGE,"E75.bottom")])]});
            var sketch = newSketch(context, id + "F33", { "sketchPlane" : qUnion([Q0])});
            skLineSegment(sketch, "E77", {"start": v(-4.18, -2.24) * mm, "end": v(-4.01, -3.2) * mm});
            skLineSegment(sketch, "E78", {"start": v(-3.38, -2.24) * mm, "end": v(-3.55, -3.2) * mm});
            skSolve(sketch);
        }
        {
            var Q0;
            Q0=makeQuery(id+"F31.opExtrude","SWEPT_FACE",FACE,{"disambiguationData":[OSD([sQuery(id+"F30.wireOp",EDGE,"E76.top")])]});
            var sketch = newSketch(context, id + "F34", { "sketchPlane" : qUnion([Q0])});
            skLineSegment(sketch, "E79", {"start": v(0.82, -2.24) * mm, "end": v(0.99, -3.2) * mm});
            skLineSegment(sketch, "E80", {"start": v(1.62, -2.24) * mm, "end": v(1.45, -3.2) * mm});
            skSolve(sketch);
        }
        {
            var Q0;
            {var subQ0=sQuery(id+"F34.wireOp",EDGE,"E80");Q0=makeQuery(id+"F34.imprint","IMPRINT",FACE,{"disambiguationData":[TD([[makeQuery(id+"F34.imprint","IMPRINT",EDGE,{"derivedFrom":subQ0}),1.0]])]});}
            var Q1;
            {var subQ0=sQuery(id+"F34.wireOp",EDGE,"E79");Q1=makeQuery(id+"F34.imprint","IMPRINT",FACE,{"disambiguationData":[TD([[makeQuery(id+"F34.imprint","IMPRINT",EDGE,{"derivedFrom":subQ0}),-1.0]])]});}
            var Q2;
            {var subQ0=sQuery(id+"F33.wireOp",EDGE,"E78");Q2=makeQuery(id+"F33.imprint","IMPRINT",FACE,{"disambiguationData":[TD([[makeQuery(id+"F33.imprint","IMPRINT",EDGE,{"derivedFrom":subQ0}),1.0]])]});}
            extrude(context, id + "F35", {"entities" : qUnion([Q0, Q1, Q2]), "operationType" : NewBodyOperationType.REMOVE, "oppositeDirection" : true, "depth" : 25 * mm, "offsetDistance" : 25 * mm});
        }
        {
            var Q0;
            {var subQ0=sQuery(id+"F33.wireOp",EDGE,"E78");Q0=makeQuery(id+"F33.imprint","IMPRINT",FACE,{"disambiguationData":[TD([[makeQuery(id+"F33.imprint","IMPRINT",EDGE,{"derivedFrom":subQ0}),1.0]])]});}
            var Q1;
            {var subQ0=sQuery(id+"F33.wireOp",EDGE,"E77");Q1=makeQuery(id+"F33.imprint","IMPRINT",FACE,{"disambiguationData":[TD([[makeQuery(id+"F33.imprint","IMPRINT",EDGE,{"derivedFrom":subQ0}),-1.0]])]});}
            extrude(context, id + "F36", {"entities" : qUnion([Q0, Q1]), "operationType" : NewBodyOperationType.REMOVE, "oppositeDirection" : true, "depth" : 25 * mm, "offsetDistance" : 25 * mm});
        }
        {
            var Q0;
            Q0=makeQuery(id+"F23.opExtrude","SWEPT_EDGE",EDGE,{"disambiguationData":[OSD([sQuery(id+"F22.wireOp",EDGE,"E58.bottom"),sQuery(id+"F22.wireOp",EDGE,"E58.left")])]});
            var Q1;
            Q1=makeQuery(id+"F23.opExtrude","SWEPT_EDGE",EDGE,{"disambiguationData":[OSD([sQuery(id+"F22.wireOp",EDGE,"E58.top"),sQuery(id+"F22.wireOp",EDGE,"E58.left")])]});
            var Q2;
            Q2=makeQuery(id+"F23.opExtrude","SWEPT_EDGE",EDGE,{"disambiguationData":[OSD([sQuery(id+"F22.wireOp",EDGE,"E58.top"),sQuery(id+"F22.wireOp",EDGE,"E58.right")])]});
            var Q3;
            Q3=makeQuery(id+"F23.opExtrude","SWEPT_EDGE",EDGE,{"disambiguationData":[OSD([sQuery(id+"F22.wireOp",EDGE,"E58.bottom"),sQuery(id+"F22.wireOp",EDGE,"E58.right")])]});
            var Q4;
            Q4=makeQuery(id+"F23.opExtrude","SWEPT_EDGE",EDGE,{"disambiguationData":[OSD([sQuery(id+"F22.wireOp",EDGE,"E59.top"),sQuery(id+"F22.wireOp",EDGE,"E59.right")])]});
            var Q5;
            Q5=makeQuery(id+"F23.opExtrude","SWEPT_EDGE",EDGE,{"disambiguationData":[OSD([sQuery(id+"F22.wireOp",EDGE,"E59.top"),sQuery(id+"F22.wireOp",EDGE,"E59.left")])]});
            var Q6;
            Q6=makeQuery(id+"F23.opExtrude","SWEPT_EDGE",EDGE,{"disambiguationData":[OSD([sQuery(id+"F22.wireOp",EDGE,"E59.bottom"),sQuery(id+"F22.wireOp",EDGE,"E59.right")])]});
            var Q7;
            Q7=makeQuery(id+"F23.opExtrude","SWEPT_EDGE",EDGE,{"disambiguationData":[OSD([sQuery(id+"F22.wireOp",EDGE,"E59.bottom"),sQuery(id+"F22.wireOp",EDGE,"E59.left")])]});
            var Q8;
            Q8=makeQuery(id+"F6.boolean.opBoolean","COPY",EDGE,{"derivedFrom":makeQuery(id+"F6.opExtrude","CAP_EDGE",EDGE,{"disambiguationData":[OSD([sQuery(id+"F0.wireOp",EDGE,"E13")])],"isStart":true})});
            var Q9;
            Q9=makeQuery(id+"F6.boolean.opBoolean","COPY",EDGE,{"derivedFrom":makeQuery(id+"F6.opExtrude","CAP_EDGE",EDGE,{"disambiguationData":[OSD([sQuery(id+"F0.wireOp",EDGE,"E14")])],"isStart":true})});
            var Q10;
            Q10=makeQuery(id+"F6.boolean.opBoolean","COPY",EDGE,{"derivedFrom":makeQuery(id+"F6.opExtrude","CAP_EDGE",EDGE,{"disambiguationData":[OSD([sQuery(id+"F0.wireOp",EDGE,"E15")])],"isStart":true})});
            var Q11;
            Q11=makeQuery(id+"F6.boolean.opBoolean","COPY",EDGE,{"derivedFrom":makeQuery(id+"F6.opExtrude","CAP_EDGE",EDGE,{"disambiguationData":[OSD([sQuery(id+"F0.wireOp",EDGE,"E16")])],"isStart":true})});
            var Q12;
            Q12=makeQuery(id+"F15.boolean.opBoolean","COPY",EDGE,{"derivedFrom":makeQuery(id+"F15.opExtrude","SWEPT_EDGE",EDGE,{"disambiguationData":[OSD([sQuery(id+"F0.wireOp",EDGE,"E32"),sQuery(id+"F14.wireOp",EDGE,"E47.MirrorCS"),sQuery(id+"F14.wireOp",EDGE,"E48")])]})});
            var Q13;
            Q13=makeQuery(id+"F15.boolean.opBoolean","COPY",EDGE,{"derivedFrom":makeQuery(id+"F15.opExtrude","SWEPT_EDGE",EDGE,{"disambiguationData":[OSD([sQuery(id+"F0.wireOp",EDGE,"E32"),sQuery(id+"F14.wireOp",EDGE,"E44"),sQuery(id+"F14.wireOp",EDGE,"E48")])]})});
            var Q14;
            Q14=makeQuery(id+"F1.opExtrude","SWEPT_EDGE",EDGE,{"disambiguationData":[OSD([sQuery(id+"F0.wireOp",EDGE,"E11"),sQuery(id+"F0.wireOp",EDGE,"E12")])]});
            var Q15;
            Q15=makeQuery(id+"F1.opExtrude","SWEPT_EDGE",EDGE,{"disambiguationData":[OSD([sQuery(id+"F0.wireOp",EDGE,"E10"),sQuery(id+"F0.wireOp",EDGE,"E11")])]});
            var Q16;
            Q16=makeQuery(id+"F1.opExtrude","SWEPT_EDGE",EDGE,{"disambiguationData":[OSD([sQuery(id+"F0.wireOp",EDGE,"E8"),sQuery(id+"F0.wireOp",EDGE,"E9")])]});
            var Q17;
            Q17=makeQuery(id+"F1.opExtrude","SWEPT_EDGE",EDGE,{"disambiguationData":[OSD([sQuery(id+"F0.wireOp",EDGE,"E4"),sQuery(id+"F0.wireOp",EDGE,"E5")])]});
            var Q18;
            Q18=makeQuery(id+"F8.boolean.opBoolean","COPY",EDGE,{"derivedFrom":makeQuery(id+"F8.opExtrude","CAP_EDGE",EDGE,{"disambiguationData":[OSD([sQuery(id+"F7.wireOp",EDGE,"E43")])],"isStart":true})});
            var Q19;
            Q19=makeQuery(id+"F5.opExtrude","CAP_EDGE",EDGE,{"disambiguationData":[OSD([sQuery(id+"F0.wireOp",EDGE,"E13")])],"isStart":false});
            var Q20;
            Q20=makeQuery(id+"F4.opExtrude","SWEPT_EDGE",EDGE,{"disambiguationData":[OSD([sQuery(id+"F0.wireOp",EDGE,"E32"),sQuery(id+"F0.wireOp",EDGE,"E33")])]});
            var Q21;
            Q21=makeQuery(id+"F4.opExtrude","SWEPT_EDGE",EDGE,{"disambiguationData":[OSD([sQuery(id+"F0.wireOp",EDGE,"E31"),sQuery(id+"F0.wireOp",EDGE,"E32")])]});
            var Q22;
            Q22=makeQuery(id+"F4.opExtrude","SWEPT_EDGE",EDGE,{"disambiguationData":[OSD([sQuery(id+"F0.wireOp",EDGE,"E30"),sQuery(id+"F0.wireOp",EDGE,"E31")])]});
            var Q23;
            Q23=makeQuery(id+"F1.opExtrude","SWEPT_EDGE",EDGE,{"disambiguationData":[OSD([sQuery(id+"F0.wireOp",EDGE,"E1"),sQuery(id+"F0.wireOp",EDGE,"E2")])]});
            var Q24;
            Q24=makeQuery(id+"F5.opExtrude","CAP_EDGE",EDGE,{"disambiguationData":[OSD([sQuery(id+"F0.wireOp",EDGE,"E14")])],"isStart":false});
            var Q25;
            Q25=makeQuery(id+"F5.opExtrude","CAP_EDGE",EDGE,{"disambiguationData":[OSD([sQuery(id+"F0.wireOp",EDGE,"E16")])],"isStart":false});
            var Q26;
            Q26=makeQuery(id+"F5.opExtrude","CAP_EDGE",EDGE,{"disambiguationData":[OSD([sQuery(id+"F0.wireOp",EDGE,"E15")])],"isStart":false});
            fillet(context, id + "F37", {"entities" : qUnion([Q0, Q1, Q2, Q3, Q4, Q5, Q6, Q7, Q8, Q9, Q10, Q11, Q12, Q13, Q14, Q15, Q16, Q17, Q18, Q19, Q20, Q21, Q22, Q23, Q24, Q25, Q26]), "radius" : 0.2 * mm, "tangentPropagation" : true, "allowEdgeOverflow" : false});
        }
    });
